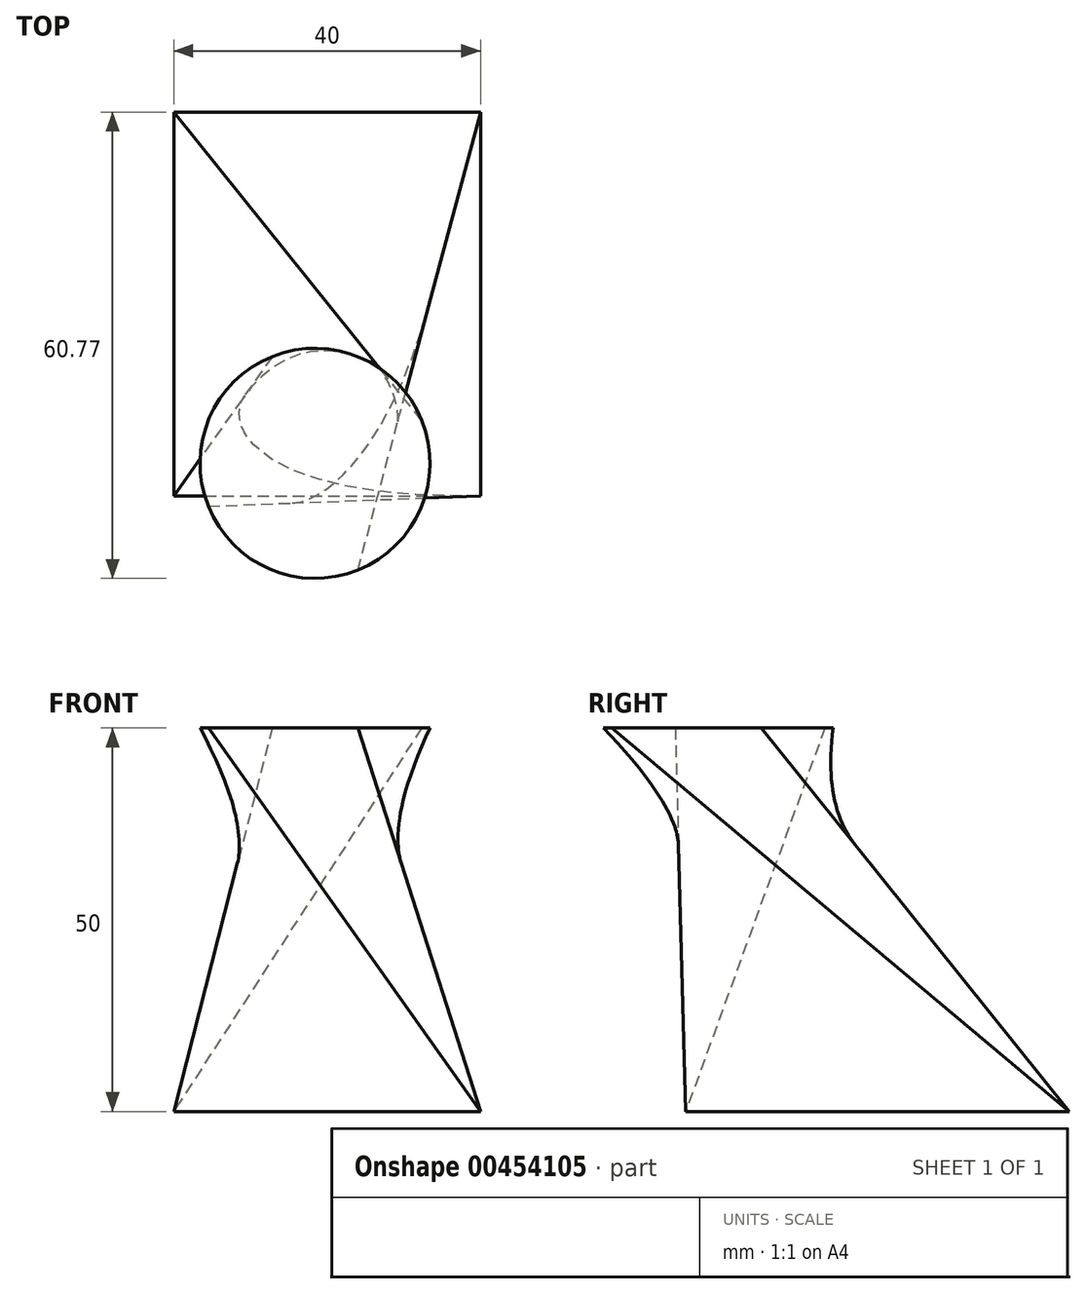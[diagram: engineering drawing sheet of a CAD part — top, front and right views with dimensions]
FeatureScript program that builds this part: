
annotation { "Feature Type Name" : "Feature", "Feature Type Description" : "" }
export const myFeature = defineFeature(function(context is Context, id is Id, definition is map)
    precondition{}
    {
        {
            var Q0;
            Q0=qCreatedBy(makeId("Top.planeOp"),FACE);
            var sketch = newSketch(context, id + "F0", { "sketchPlane" : qUnion([Q0])});
            skLineSegment(sketch, "E0.bottom", {"start": v(0, 0) * mm, "end": v(40, 0) * mm});
            skLineSegment(sketch, "E0.top", {"start": v(0, -50) * mm, "end": v(40, -50) * mm});
            skLineSegment(sketch, "E0.left", {"start": v(0, 0) * mm, "end": v(0, -50) * mm});
            skLineSegment(sketch, "E0.right", {"start": v(40, 0) * mm, "end": v(40, -50) * mm});
            skSolve(sketch);
        }
        {
            var Q0;
            Q0=qCreatedBy(makeId("Top.planeOp"),FACE);
            cPlane(context, id + "F1", {"entities" : qUnion([Q0]), "cplaneType" : CPlaneType.OFFSET, "offset" : 50 * mm, "width" : 150 * mm, "height" : 150 * mm});
        }
        {
            var Q0;
            Q0=qCreatedBy(id+"F1.planeOp",FACE);
            var sketch = newSketch(context, id + "F2", { "sketchPlane" : qUnion([Q0])});
            skCircle(sketch, "E1", {"center": v(18.41, -45.77) * mm, "radius": 15 * mm});
            skSolve(sketch);
        }
        {
            var Q0;
            Q0 = qSketchRegion(id + "F2", true);
            var Q1;
            Q1 = qSketchRegion(id + "F0", true);
            loft(context, id + "F3", {"sheetProfilesArray" : [{ "sheetProfileEntities" : qUnion([Q0]) }, { "sheetProfileEntities" : qUnion([Q1]) }]});
        }
    });
